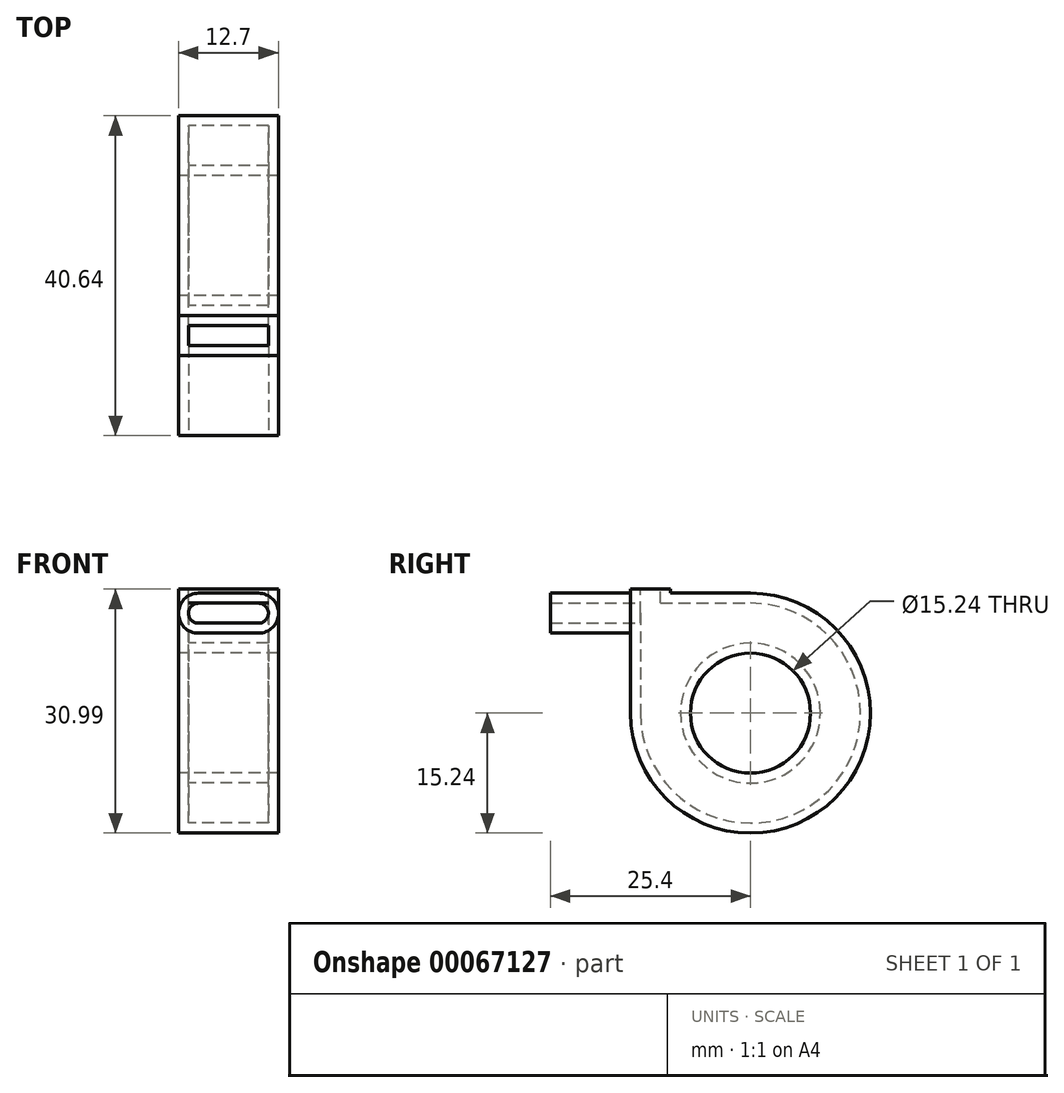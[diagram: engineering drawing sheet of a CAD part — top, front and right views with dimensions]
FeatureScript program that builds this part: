
annotation { "Feature Type Name" : "Feature", "Feature Type Description" : "" }
export const myFeature = defineFeature(function(context is Context, id is Id, definition is map)
    precondition{}
    {
        {
            var Q0;
            Q0=qCreatedBy(makeId("Right.planeOp"),FACE);
            var sketch = newSketch(context, id + "F0", { "sketchPlane" : qUnion([Q0])});
            skLineSegment(sketch, "E0", {"start": v(-25.4, 15.24) * mm, "end": v(0, 15.24) * mm});
            skArc(sketch, "E1", {"start": v(-15.24, 0) * mm, "mid": v(10.78, -10.78) * mm, "end": v(0, 15.24) * mm});
            skLineSegment(sketch, "E2", {"start": v(-25.4, 15.24) * mm, "end": v(-25.4, 10.16) * mm});
            skLineSegment(sketch, "E3", {"start": v(-25.4, 10.16) * mm, "end": v(-15.24, 10.16) * mm});
            skLineSegment(sketch, "E4", {"start": v(-15.24, 10.16) * mm, "end": v(-15.24, 0) * mm});
            skLineSegment(sketch, "E5.top", {"start": v(-15.24, 15.75) * mm, "end": v(-10.16, 15.75) * mm});
            skLineSegment(sketch, "E5.left", {"start": v(-15.24, 15.24) * mm, "end": v(-15.24, 15.75) * mm});
            skLineSegment(sketch, "E5.right", {"start": v(-10.16, 15.24) * mm, "end": v(-10.16, 15.75) * mm});
            skCircle(sketch, "E6", {"center": v(0, 0) * mm, "radius": 7.62 * mm});
            skSolve(sketch);
        }
        {
            var Q0;
            Q0 = qSketchRegion(id + "F0", true);
            extrude(context, id + "F1", {"entities" : qUnion([Q0]), "endBound" : BoundingType.SYMMETRIC, "depth" : 12.7 * mm});
        }
        {
            var Q0;
            Q0=makeQuery(id+"F1.opExtrude","SWEPT_FACE",FACE,{"disambiguationData":[OSD([sQuery(id+"F0.wireOp",EDGE,"E2")])]});
            var Q1;
            Q1=makeQuery(id+"F1.opExtrude","SWEPT_FACE",FACE,{"disambiguationData":[OSD([sQuery(id+"F0.wireOp",EDGE,"E5.top")])]});
            shell(context, id + "F2", {"entities" : qUnion([Q0, Q1]), "thickness" : 1.27 * mm});
        }
        {
            var Q0;
            {var subQ0=sQuery(id+"F0.wireOp",EDGE,"E0");Q0=makeQuery(id+"F1.opExtrude","CAP_EDGE",EDGE,{"disambiguationData":[OSD([subQ0]),TDD([makeQuery(id+"F0.imprint","IMPRINT",EDGE,{"disambiguationData":[TD([[makeQuery(id+"F0.imprint","INTERSECT",VERTEX,{"derivedFrom":[subQ0,sQuery(id+"F0.wireOp",EDGE,"E2")]}),-1.0]])],"derivedFrom":subQ0})])],"isStart":true});}
            var Q1;
            Q1=makeQuery(id+"F1.opExtrude","CAP_EDGE",EDGE,{"disambiguationData":[OSD([sQuery(id+"F0.wireOp",EDGE,"E3")])],"isStart":true});
            var Q2;
            {var subQ0=sQuery(id+"F0.wireOp",EDGE,"E0");Q2=makeQuery(id+"F1.opExtrude","CAP_EDGE",EDGE,{"disambiguationData":[OSD([subQ0]),TDD([makeQuery(id+"F0.imprint","IMPRINT",EDGE,{"disambiguationData":[TD([[makeQuery(id+"F0.imprint","INTERSECT",VERTEX,{"derivedFrom":[subQ0,sQuery(id+"F0.wireOp",EDGE,"E2")]}),-1.0]])],"derivedFrom":subQ0})])],"isStart":false});}
            var Q3;
            Q3=makeQuery(id+"F1.opExtrude","CAP_EDGE",EDGE,{"disambiguationData":[OSD([sQuery(id+"F0.wireOp",EDGE,"E3")])],"isStart":false});
            fillet(context, id + "F3", {"entities" : qUnion([Q0, Q1, Q2, Q3]), "radius" : 2.54 * mm, "tangentPropagation" : true, "allowEdgeOverflow" : false});
        }
        {
            var Q0;
            {var subQ0=sQuery(id+"F0.wireOp",EDGE,"E3");Q0=makeQuery(id+"F2.opShell","OFFSET_EDGE",EDGE,{"disambiguationData":[OSD([subQ0]),TDD([makeQuery(id+"F1.opExtrude","CAP_EDGE",EDGE,{"disambiguationData":[OSD([subQ0])],"isStart":true})])]});}
            var Q1;
            {var subQ0=sQuery(id+"F0.wireOp",EDGE,"E0");Q1=makeQuery(id+"F2.opShell","OFFSET_EDGE",EDGE,{"disambiguationData":[OSD([subQ0]),TDD([makeQuery(id+"F1.opExtrude","CAP_EDGE",EDGE,{"disambiguationData":[OSD([subQ0]),TDD([makeQuery(id+"F0.imprint","IMPRINT",EDGE,{"disambiguationData":[TD([[makeQuery(id+"F0.imprint","INTERSECT",VERTEX,{"derivedFrom":[subQ0,sQuery(id+"F0.wireOp",EDGE,"E2")]}),-1.0]])],"derivedFrom":subQ0})])],"isStart":true})])]});}
            var Q2;
            {var subQ0=sQuery(id+"F0.wireOp",EDGE,"E0");Q2=makeQuery(id+"F2.opShell","OFFSET_EDGE",EDGE,{"disambiguationData":[OSD([subQ0]),TDD([makeQuery(id+"F1.opExtrude","CAP_EDGE",EDGE,{"disambiguationData":[OSD([subQ0]),TDD([makeQuery(id+"F0.imprint","IMPRINT",EDGE,{"disambiguationData":[TD([[makeQuery(id+"F0.imprint","INTERSECT",VERTEX,{"derivedFrom":[subQ0,sQuery(id+"F0.wireOp",EDGE,"E2")]}),-1.0]])],"derivedFrom":subQ0})])],"isStart":false})])]});}
            var Q3;
            {var subQ0=sQuery(id+"F0.wireOp",EDGE,"E3");Q3=makeQuery(id+"F2.opShell","OFFSET_EDGE",EDGE,{"disambiguationData":[OSD([subQ0]),TDD([makeQuery(id+"F1.opExtrude","CAP_EDGE",EDGE,{"disambiguationData":[OSD([subQ0])],"isStart":false})])]});}
            fillet(context, id + "F4", {"entities" : qUnion([Q0, Q1, Q2, Q3]), "radius" : 1.27 * mm, "tangentPropagation" : true, "allowEdgeOverflow" : false});
        }
    });
